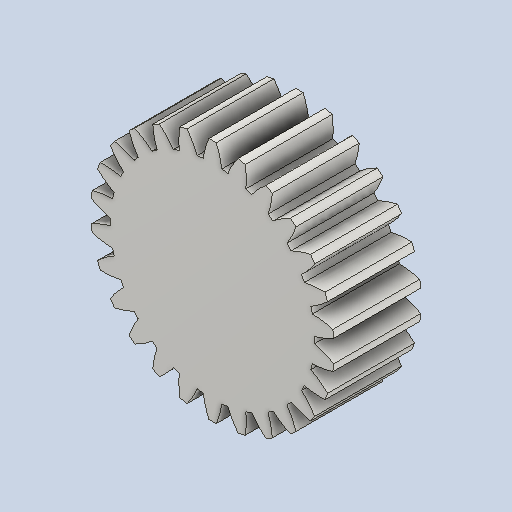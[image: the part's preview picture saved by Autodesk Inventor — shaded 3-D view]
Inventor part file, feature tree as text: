
AUTODESK INVENTOR PART (.ipt)
format: ipt  version: 2024 (Build 280153000, 153)  size: 269,824 bytes
history: native  units: mm (DEFAULTED — no unit token found)
features: plane x3, other x3, extrude x1, sketch x1
ambient origin geometry x8: Origin, YZ Plane, XZ Plane, XY Plane, X Axis, Y Axis, Z Axis, Center Point
bodies: Solid1 (feature_tree)
feature tree (8):
  extrude  "Extrusion1"  Depth=20.0mm TaperAngle=0.0deg
  plane  "Work Plane2"
  plane  "Work Plane8"
  plane  "Work Plane9"
  other  "Spur Gear"
  sketch  "Sketch1"  dims[d0=56.0mm d1=20.0mm d2=0.0mm d3=52.0mm d4=10.0mm d5=0.0mm d16=36.0mm d17=0.0mm d34=1.208305mm d39=0.0mm d41=0.0mm d43=36.0mm d46=36.0mm d47=0.0mm d48=0.0mm]
  other  "Srf1"
  other  "Pitch Diameter"
